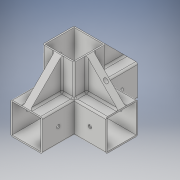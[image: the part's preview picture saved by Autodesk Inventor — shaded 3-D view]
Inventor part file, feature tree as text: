
AUTODESK INVENTOR PART (.ipt)
format: ipt  version: 2019.4 (Build 234330000, 330)  size: 306,688 bytes
history: native  units: in
note: dims shown in document units (in); Inventor stores cm internally (conversion verified against a paired STEP export)
features: extrude x7, sketch x5, chamfer x2, hole x2, fillet x2
ambient origin geometry x8: Origin, YZ Plane, XZ Plane, XY Plane, X Axis, Y Axis, Z Axis, Center Point
bodies: Solid1 (feature_tree)
feature tree (18):
  extrude  "Extrusion1"  Depth=1.6142in
  sketch  "Sketch2"  dims[d2=1.7717in d3=1.7717in]
  extrude  "Extrusion2"  Depth=1.7717in
  extrude  "Extrusion3"  Depth=1.6142in
  sketch  "Sketch3"  dims[d4=5.315in d5=0.0in d6=1.6142in]
  extrude  "Extrusion4"  Depth=1.7717in
  extrude  "Extrusion5"  Depth=0.0984in TaperAngle=0.0deg
  extrude  "Extrusion6"  Depth=0.0984in TaperAngle=0.0deg
  chamfer  "Chamfer1"  Distance=1.6142in
  extrude  "Extrusion7"  Depth=0.0984in
  chamfer  "Chamfer2"  Distance=1.7717in
  hole  "Hole1"  [1 undecoded]
  hole  "Hole2"  [1 undecoded]
  fillet  "Fillet2"  Radius=1.5748in
  fillet  "Fillet3"  Radius=0.3937in
  sketch  "Sketch1"  dims[d0=1.6142in d1=1.6142in]
  sketch  "Sketch4"  dims[d7=1.6142in d8=1.7717in]
  sketch  "Sketch5"  dims[d9=1.7717in d10=1.7717in d11=0.0in d12=1.5748in d13=0.0in d14=1.6142in d15=1.6142in d16=1.7717in d17=1.7717in d18=1.7717in d19=0.0in d20=1.5748in d21=0.0in d22=0.3937in d23=0.1969in d24=0.3937in d25=0.1969in d26=1.7717in d27=0.0in d28=1.7717in d29=0.0787in d30=45.0deg d31=0.1969in d32=0.3937in d33=1.7717in d34=0.0in d35=1.7717in d36=0.0787in d37=45.0deg d39=0.1969in d40=0.2362in d41=0.1575in d42=0.0787in d43=90.0deg d44=0.315in d45=0.8108in d46=0.1969in d47=0.2362in d48=0.1575in d49=0.0787in d50=90.0deg d51=0.315in d52=0.8108in d53=0.0984in d54=0.0984in]
note: 2 required parameter values undecoded (feature->parameter linkage not recoverable at this tier; creation-order binding heuristic only, values carry confidence <= 0.55)
